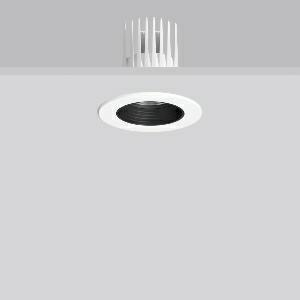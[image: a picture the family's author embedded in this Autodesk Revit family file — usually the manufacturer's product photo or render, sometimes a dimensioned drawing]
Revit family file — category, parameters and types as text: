
# Revit family: heledon_mini_e_901752_002_2_76_4482
name_source: partatom
category: Lighting Fixtures
units: mm (PartAtom-declared; Revit-internal decimal feet)

## family parameters
Cut with Voids When Loaded = No
Host = Face
Light Source = No
Part Type = Normal
Room Calculation Point = No
Round Connector Dimension = Use Diameter
Shared = No

## types (1)
- HELEDON mini E (1 x LED Modul 927, 2850 lm, 2700)
    Apparent Load = 29 VA
    Approval mark = CE
    CIE Flux Codes = 96 100 100 100 100
    Color Rendering = 92
    Color Temperature = 2700
    Default Elevation = 1800 mm
    Description = Series: HELEDON mini
Round recessed downlight. Housing: die-cast aluminium, powder-coated. Black plastic ring and recessed LED to prevent glare from the side. Optical assembly with lens made of plastic (polycarbonate) for the best homogeneous light distribution - can be changed without tools. Best colour rendering index Ra>90. Suitable for Recessed ceiling mounting. Installation without tools thanks to spring fastening system. Including separate LED converter with connecting cable 600 mm.High quality converter without flickering and stroboscopic effect. Through-wiring box (5 pole) available as accessory. The following accessories can be mounted without use of tools: interchangeable lenses, decorative glasses, honeycomb louvre, clear and frosted diffusers, white interchangeable plastic ring. 
Colour: traffic white, matt (RAL 9016)
Diameter: 124 mm
Height: 3 mm
Cut-out diameter: 114 mm
Recess height: 170 mm
Luminaire: recess height: 120 mm
Lamp: LED
Socket: without socket
Colour temperature: 2700K
Colour rendering index (CRI): 92
System power: 29 W
Rated luminous flux: 2850 lm
Luminous efficiency: 98 lm/W
Control gear: Converter, dimmable, DALI
Protection class: II
Type of protection: IP 20
    Height = 0 mm  [stored 0 ft]
    Lamp = 1 x LED Modul 927
    Lamp Light Flux = 2850 lm
    Lamp count = 1
    Length = 124 mm  [stored 0.406824 ft]
    Lifetime = 50000 h
    Luminous efficacy = 98 lm/W
    Manufacturer = RZB
    ModVariant = No
    Model = 901752.002.2.76
    Mounting Place = Ceiling
    Mounting Type = Recessed
    Number of Poles = 1
    OnlyDefault = Yes
    Power Factor = 1
    Product Name = HELEDON mini E
    Product group = Recessed downlights
    ProductGroupID = 402
    Protection Class = Protection class II
    Protection Degree = IP 20
    RLX_Detail_Level = 1
    RLX_Emergency_Light_Flux = 0 lm
    RLX_Emergency_Type = 0
    RLX_Emergency_Type_DB = No
    RlxData = <blob elided: 124601 chars, md5=dd4ab878>
    Socket = socket
    Standby Power = 0 W
    System Light Flux = 2850 lm
    System Power = 29 W
    Type Comments = Product without accessories
    Type Image = 901656.002.jpg
    URL = http://relux.com
    VarID = ---
    Voltage = 230 V
    Voltage Range = 220-240 V
    Weight = 0.00 kg
    Width = 0 mm  [stored 0 ft]

note: [stored X ft] marks values corroborated as IEEE doubles in the binary element streams (Revit-internal decimal feet)

## geometry (parser evidence)
native form markers: Blend x4, Sweep x11
no freeform markers — native parametric forms only
